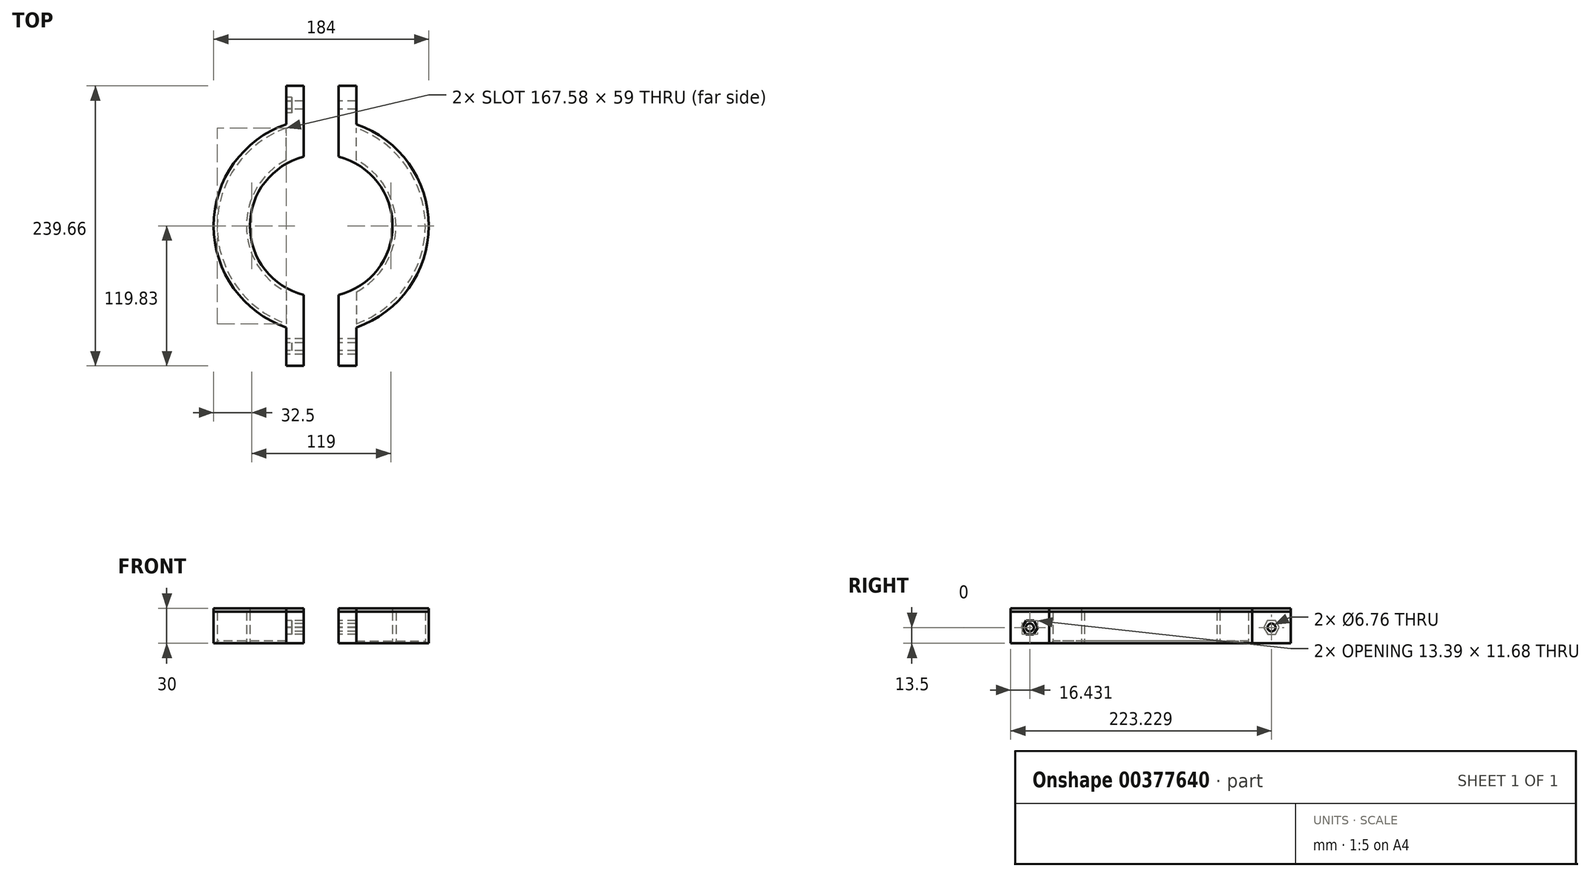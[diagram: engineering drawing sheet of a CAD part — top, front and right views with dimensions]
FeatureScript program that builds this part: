
annotation { "Feature Type Name" : "Feature", "Feature Type Description" : "" }
export const myFeature = defineFeature(function(context is Context, id is Id, definition is map)
    precondition{}
    {
        {
            var Q0;
            Q0=qCreatedBy(makeId("Top.planeOp"),FACE);
            var sketch = newSketch(context, id + "F0", { "sketchPlane" : qUnion([Q0])});
            skCircle(sketch, "E0", {"center": v(0, 0) * mm, "radius": 57 * mm, "construction": true});
            skCircle(sketch, "E1.0", {"center": v(0, 0) * mm, "radius": 61 * mm});
            skCircle(sketch, "E2.0", {"center": v(0, 0) * mm, "radius": 64 * mm});
            skCircle(sketch, "E3.0", {"center": v(0, 0) * mm, "radius": 89 * mm});
            skCircle(sketch, "E4.0", {"center": v(0, 0) * mm, "radius": 92 * mm});
            skLineSegment(sketch, "E5", {"start": v(0, 0) * mm, "end": v(0, 92) * mm, "construction": true});
            skLineSegment(sketch, "E6", {"start": v(0, 0) * mm, "end": v(0, -92) * mm, "construction": true});
            skLineSegment(sketch, "E7", {"start": v(-57, 0) * mm, "end": v(0, 0) * mm, "construction": true});
            skLineSegment(sketch, "E8", {"start": v(0, 0) * mm, "end": v(57, 0) * mm, "construction": true});
            skLineSegment(sketch, "E9", {"start": v(-15, 59.13) * mm, "end": v(-15, 90.77) * mm});
            skLineSegment(sketch, "E10", {"start": v(-30, 53.11) * mm, "end": v(-30, 86.97) * mm});
            skLineSegment(sketch, "E11", {"start": v(15, 59.13) * mm, "end": v(15, 90.77) * mm});
            skLineSegment(sketch, "E12", {"start": v(30, 53.11) * mm, "end": v(30, 86.97) * mm});
            skLineSegment(sketch, "E13", {"start": v(-30, 80.88) * mm, "end": v(-15, 80.88) * mm, "construction": true});
            skLineSegment(sketch, "E14", {"start": v(15, 80.88) * mm, "end": v(30, 80.88) * mm, "construction": true});
            skLineSegment(sketch, "E15", {"start": v(-15, 80.88) * mm, "end": v(0, 80.88) * mm, "construction": true});
            skLineSegment(sketch, "E16", {"start": v(0, 80.88) * mm, "end": v(15, 80.88) * mm, "construction": true});
            skLineSegment(sketch, "E17", {"start": v(-30, 86.97) * mm, "end": v(-30, 119.83) * mm});
            skLineSegment(sketch, "E18", {"start": v(-30, 119.83) * mm, "end": v(-15, 119.83) * mm});
            skLineSegment(sketch, "E19", {"start": v(-15, 119.83) * mm, "end": v(-15, 90.77) * mm});
            skLineSegment(sketch, "E20", {"start": v(15, 90.77) * mm, "end": v(15, 119.83) * mm});
            skLineSegment(sketch, "E21", {"start": v(15, 119.83) * mm, "end": v(30, 119.83) * mm});
            skLineSegment(sketch, "E22", {"start": v(30, 119.83) * mm, "end": v(30, 86.97) * mm});
            skLineSegment(sketch, "E23.MirrorCS", {"start": v(-15, -119.83) * mm, "end": v(-15, -90.77) * mm});
            skLineSegment(sketch, "E24.MirrorCS", {"start": v(-30, -86.97) * mm, "end": v(-30, -119.83) * mm});
            skLineSegment(sketch, "E25.MirrorCS", {"start": v(-30, -119.83) * mm, "end": v(-15, -119.83) * mm});
            skLineSegment(sketch, "E26.MirrorCS", {"start": v(15, -90.77) * mm, "end": v(15, -119.83) * mm});
            skLineSegment(sketch, "E27.MirrorCS", {"start": v(15, -119.83) * mm, "end": v(30, -119.83) * mm});
            skLineSegment(sketch, "E28.MirrorCS", {"start": v(30, -119.83) * mm, "end": v(30, -86.97) * mm});
            skLineSegment(sketch, "E29.MirrorCS", {"start": v(15, -59.13) * mm, "end": v(15, -90.77) * mm});
            skLineSegment(sketch, "E30.MirrorCS", {"start": v(30, -53.11) * mm, "end": v(30, -86.97) * mm});
            skLineSegment(sketch, "E31.MirrorCS", {"start": v(-15, -59.13) * mm, "end": v(-15, -90.77) * mm});
            skLineSegment(sketch, "E32.MirrorCS", {"start": v(-30, -53.11) * mm, "end": v(-30, -86.97) * mm});
            skSolve(sketch);
        }
        {
            var Q0;
            {var subQ0=sQuery(id+"F0.wireOp",EDGE,"E10");var subQ1=sQuery(id+"F0.wireOp",EDGE,"E2.0");var subQ2=makeQuery(id+"F0.imprint","INTERSECT",VERTEX,{"derivedFrom":[subQ1,subQ0]});Q0=makeQuery(id+"F0.imprint","IMPRINT",FACE,{"disambiguationData":[TD([[makeQuery(id+"F0.imprint","IMPRINT",EDGE,{"disambiguationData":[TD([[subQ2,-1.0]])],"derivedFrom":subQ1}),-1.0]])]});}
            var Q1;
            {var subQ0=sQuery(id+"F0.wireOp",EDGE,"E12");var subQ1=sQuery(id+"F0.wireOp",EDGE,"E2.0");var subQ2=makeQuery(id+"F0.imprint","INTERSECT",VERTEX,{"derivedFrom":[subQ1,subQ0]});Q1=makeQuery(id+"F0.imprint","IMPRINT",FACE,{"disambiguationData":[TD([[makeQuery(id+"F0.imprint","IMPRINT",EDGE,{"disambiguationData":[TD([[subQ2,1.0]])],"derivedFrom":subQ1}),-1.0]])]});}
            extrude(context, id + "F1", {"entities" : qUnion([Q0, Q1]), "oppositeDirection" : true, "depth" : 2 * mm, "offsetDistance" : 25 * mm});
        }
        {
            var Q0;
            {var subQ0=sQuery(id+"F0.wireOp",EDGE,"E10");var subQ1=sQuery(id+"F0.wireOp",EDGE,"E1.0");var subQ2=makeQuery(id+"F0.imprint","INTERSECT",VERTEX,{"derivedFrom":[subQ1,subQ0]});Q0=makeQuery(id+"F0.imprint","IMPRINT",FACE,{"disambiguationData":[TD([[makeQuery(id+"F0.imprint","IMPRINT",EDGE,{"disambiguationData":[TD([[subQ2,-1.0]])],"derivedFrom":subQ1}),-1.0]])]});}
            var Q1;
            {var subQ0=sQuery(id+"F0.wireOp",EDGE,"E9");var subQ1=sQuery(id+"F0.wireOp",EDGE,"E1.0");var subQ2=makeQuery(id+"F0.imprint","INTERSECT",VERTEX,{"derivedFrom":[subQ1,subQ0]});Q1=makeQuery(id+"F0.imprint","IMPRINT",FACE,{"disambiguationData":[TD([[makeQuery(id+"F0.imprint","IMPRINT",EDGE,{"disambiguationData":[TD([[subQ2,-1.0]])],"derivedFrom":subQ1}),-1.0]])]});}
            var Q2;
            {var subQ0=sQuery(id+"F0.wireOp",EDGE,"E11");var subQ1=sQuery(id+"F0.wireOp",EDGE,"E1.0");var subQ2=makeQuery(id+"F0.imprint","INTERSECT",VERTEX,{"derivedFrom":[subQ1,subQ0]});Q2=makeQuery(id+"F0.imprint","IMPRINT",FACE,{"disambiguationData":[TD([[makeQuery(id+"F0.imprint","IMPRINT",EDGE,{"disambiguationData":[TD([[subQ2,1.0]])],"derivedFrom":subQ1}),-1.0]])]});}
            var Q3;
            {var subQ0=sQuery(id+"F0.wireOp",EDGE,"E12");var subQ1=sQuery(id+"F0.wireOp",EDGE,"E1.0");var subQ2=makeQuery(id+"F0.imprint","INTERSECT",VERTEX,{"derivedFrom":[subQ1,subQ0]});Q3=makeQuery(id+"F0.imprint","IMPRINT",FACE,{"disambiguationData":[TD([[makeQuery(id+"F0.imprint","IMPRINT",EDGE,{"disambiguationData":[TD([[subQ2,1.0]])],"derivedFrom":subQ1}),-1.0]])]});}
            var Q4;
            {var subQ0=sQuery(id+"F0.wireOp",EDGE,"E32.MirrorCS");var subQ1=sQuery(id+"F0.wireOp",EDGE,"E2.0");var subQ2=makeQuery(id+"F0.imprint","INTERSECT",VERTEX,{"derivedFrom":[subQ1,subQ0]});Q4=makeQuery(id+"F0.imprint","IMPRINT",FACE,{"disambiguationData":[TD([[makeQuery(id+"F0.imprint","IMPRINT",EDGE,{"disambiguationData":[TD([[subQ2,-1.0]])],"derivedFrom":subQ1}),-1.0]])]});}
            var Q5;
            {var subQ0=sQuery(id+"F0.wireOp",EDGE,"E31.MirrorCS");var subQ1=sQuery(id+"F0.wireOp",EDGE,"E1.0");var subQ2=makeQuery(id+"F0.imprint","INTERSECT",VERTEX,{"derivedFrom":[subQ1,subQ0]});Q5=makeQuery(id+"F0.imprint","IMPRINT",FACE,{"disambiguationData":[TD([[makeQuery(id+"F0.imprint","IMPRINT",EDGE,{"disambiguationData":[TD([[subQ2,1.0]])],"derivedFrom":subQ1}),-1.0]])]});}
            var Q6;
            {var subQ0=sQuery(id+"F0.wireOp",EDGE,"E29.MirrorCS");var subQ1=sQuery(id+"F0.wireOp",EDGE,"E2.0");var subQ2=makeQuery(id+"F0.imprint","INTERSECT",VERTEX,{"derivedFrom":[subQ1,subQ0]});Q6=makeQuery(id+"F0.imprint","IMPRINT",FACE,{"disambiguationData":[TD([[makeQuery(id+"F0.imprint","IMPRINT",EDGE,{"disambiguationData":[TD([[subQ2,-1.0]])],"derivedFrom":subQ1}),-1.0]])]});}
            var Q7;
            {var subQ0=sQuery(id+"F0.wireOp",EDGE,"E29.MirrorCS");var subQ1=sQuery(id+"F0.wireOp",EDGE,"E1.0");var subQ2=makeQuery(id+"F0.imprint","INTERSECT",VERTEX,{"derivedFrom":[subQ1,subQ0]});Q7=makeQuery(id+"F0.imprint","IMPRINT",FACE,{"disambiguationData":[TD([[makeQuery(id+"F0.imprint","IMPRINT",EDGE,{"disambiguationData":[TD([[subQ2,-1.0]])],"derivedFrom":subQ1}),-1.0]])]});}
            var Q8;
            {var subQ0=sQuery(id+"F0.wireOp",EDGE,"E29.MirrorCS");var subQ1=sQuery(id+"F0.wireOp",EDGE,"E3.0");var subQ2=makeQuery(id+"F0.imprint","INTERSECT",VERTEX,{"derivedFrom":[subQ1,subQ0]});Q8=makeQuery(id+"F0.imprint","IMPRINT",FACE,{"disambiguationData":[TD([[makeQuery(id+"F0.imprint","IMPRINT",EDGE,{"disambiguationData":[TD([[subQ2,-1.0]])],"derivedFrom":subQ1}),-1.0]])]});}
            var Q9;
            {var subQ0=sQuery(id+"F0.wireOp",EDGE,"E32.MirrorCS");var subQ1=sQuery(id+"F0.wireOp",EDGE,"E3.0");var subQ2=makeQuery(id+"F0.imprint","INTERSECT",VERTEX,{"derivedFrom":[subQ1,subQ0]});Q9=makeQuery(id+"F0.imprint","IMPRINT",FACE,{"disambiguationData":[TD([[makeQuery(id+"F0.imprint","IMPRINT",EDGE,{"disambiguationData":[TD([[subQ2,-1.0]])],"derivedFrom":subQ1}),-1.0]])]});}
            var Q10;
            {var subQ0=sQuery(id+"F0.wireOp",EDGE,"E23.MirrorCS");Q10=makeQuery(id+"F0.imprint","IMPRINT",FACE,{"disambiguationData":[TD([[makeQuery(id+"F0.imprint","IMPRINT",EDGE,{"derivedFrom":subQ0}),1.0]])]});}
            var Q11;
            {var subQ0=sQuery(id+"F0.wireOp",EDGE,"E10");var subQ1=sQuery(id+"F0.wireOp",EDGE,"E3.0");var subQ2=makeQuery(id+"F0.imprint","INTERSECT",VERTEX,{"derivedFrom":[subQ1,subQ0]});Q11=makeQuery(id+"F0.imprint","IMPRINT",FACE,{"disambiguationData":[TD([[makeQuery(id+"F0.imprint","IMPRINT",EDGE,{"disambiguationData":[TD([[subQ2,-1.0]])],"derivedFrom":subQ1}),-1.0]])]});}
            var Q12;
            {var subQ0=sQuery(id+"F0.wireOp",EDGE,"E12");var subQ1=sQuery(id+"F0.wireOp",EDGE,"E3.0");var subQ2=makeQuery(id+"F0.imprint","INTERSECT",VERTEX,{"derivedFrom":[subQ1,subQ0]});Q12=makeQuery(id+"F0.imprint","IMPRINT",FACE,{"disambiguationData":[TD([[makeQuery(id+"F0.imprint","IMPRINT",EDGE,{"disambiguationData":[TD([[subQ2,1.0]])],"derivedFrom":subQ1}),-1.0]])]});}
            var Q13;
            {var subQ0=sQuery(id+"F0.wireOp",EDGE,"E26.MirrorCS");Q13=makeQuery(id+"F0.imprint","IMPRINT",FACE,{"disambiguationData":[TD([[makeQuery(id+"F0.imprint","IMPRINT",EDGE,{"derivedFrom":subQ0}),1.0]])]});}
            var Q14;
            {var subQ0=sQuery(id+"F0.wireOp",EDGE,"E11");var subQ1=sQuery(id+"F0.wireOp",EDGE,"E2.0");var subQ2=makeQuery(id+"F0.imprint","INTERSECT",VERTEX,{"derivedFrom":[subQ1,subQ0]});Q14=makeQuery(id+"F0.imprint","IMPRINT",FACE,{"disambiguationData":[TD([[makeQuery(id+"F0.imprint","IMPRINT",EDGE,{"disambiguationData":[TD([[subQ2,1.0]])],"derivedFrom":subQ1}),-1.0]])]});}
            var Q15;
            {var subQ0=sQuery(id+"F0.wireOp",EDGE,"E20");Q15=makeQuery(id+"F0.imprint","IMPRINT",FACE,{"disambiguationData":[TD([[makeQuery(id+"F0.imprint","IMPRINT",EDGE,{"derivedFrom":subQ0}),-1.0]])]});}
            var Q16;
            {var subQ0=sQuery(id+"F0.wireOp",EDGE,"E11");var subQ1=sQuery(id+"F0.wireOp",EDGE,"E3.0");var subQ2=makeQuery(id+"F0.imprint","INTERSECT",VERTEX,{"derivedFrom":[subQ1,subQ0]});Q16=makeQuery(id+"F0.imprint","IMPRINT",FACE,{"disambiguationData":[TD([[makeQuery(id+"F0.imprint","IMPRINT",EDGE,{"disambiguationData":[TD([[subQ2,1.0]])],"derivedFrom":subQ1}),-1.0]])]});}
            var Q17;
            {var subQ0=sQuery(id+"F0.wireOp",EDGE,"E9");var subQ1=sQuery(id+"F0.wireOp",EDGE,"E2.0");var subQ2=makeQuery(id+"F0.imprint","INTERSECT",VERTEX,{"derivedFrom":[subQ1,subQ0]});Q17=makeQuery(id+"F0.imprint","IMPRINT",FACE,{"disambiguationData":[TD([[makeQuery(id+"F0.imprint","IMPRINT",EDGE,{"disambiguationData":[TD([[subQ2,-1.0]])],"derivedFrom":subQ1}),-1.0]])]});}
            var Q18;
            {var subQ0=sQuery(id+"F0.wireOp",EDGE,"E9");var subQ1=sQuery(id+"F0.wireOp",EDGE,"E3.0");var subQ2=makeQuery(id+"F0.imprint","INTERSECT",VERTEX,{"derivedFrom":[subQ1,subQ0]});Q18=makeQuery(id+"F0.imprint","IMPRINT",FACE,{"disambiguationData":[TD([[makeQuery(id+"F0.imprint","IMPRINT",EDGE,{"disambiguationData":[TD([[subQ2,-1.0]])],"derivedFrom":subQ1}),-1.0]])]});}
            var Q19;
            {var subQ2=sQuery(id+"F0.wireOp",EDGE,"E17");Q19=makeQuery(id+"F0.imprint","IMPRINT",FACE,{"disambiguationData":[TD([[makeQuery(id+"F0.imprint","IMPRINT",EDGE,{"derivedFrom":subQ2}),-1.0]])]});}
            extrude(context, id + "F2", {"entities" : qUnion([Q0, Q1, Q2, Q3, Q4, Q5, Q6, Q7, Q8, Q9, Q10, Q11, Q12, Q13, Q14, Q15, Q16, Q17, Q18, Q19]), "depth" : 25 * mm, "offsetDistance" : 25 * mm, "hasSecondDirection" : true, "secondDirectionOppositeDirection" : true, "secondDirectionDepth" : 2 * mm});
        }
        {
            var Q0;
            Q0=qCreatedBy(makeId("Right.planeOp"),FACE);
            var sketch = newSketch(context, id + "F3", { "sketchPlane" : qUnion([Q0])});
            skLineSegment(sketch, "E33", {"start": v(0, 0) * mm, "end": v(0, -64.4) * mm, "construction": true});
            skLineSegment(sketch, "E34", {"start": v(0, 0) * mm, "end": v(0, 59.15) * mm, "construction": true});
            skSolve(sketch);
        }
        {
            var Q0;
            Q0=makeQuery(id+"F2.opExtrude","SWEPT_FACE",FACE,{"disambiguationData":[OSD([sQuery(id+"F0.wireOp",EDGE,"E17")])]});
            var sketch = newSketch(context, id + "F4", { "sketchPlane" : qUnion([Q0])});
            skCircle(sketch, "E35", {"center": v(-103.4, 11.5) * mm, "radius": 3.38 * mm});
            skPoint(sketch, "E35.centerSnap0", {"position": v(-103.4, 25) * mm});
            skPoint(sketch, "E35.centerSnap1", {"position": v(-119.83, 11.5) * mm});
            skCircle(sketch, "E36.cCircle", {"center": v(-103.4, 11.5) * mm, "radius": 6.7 * mm, "construction": true});
            skLineSegment(sketch, "E36.0", {"start": v(-99.98, 17.26) * mm, "end": v(-96.7, 11.42) * mm});
            skLineSegment(sketch, "E36.1", {"start": v(-96.7, 11.42) * mm, "end": v(-100.12, 5.66) * mm});
            skLineSegment(sketch, "E36.2", {"start": v(-100.12, 5.66) * mm, "end": v(-106.82, 5.74) * mm});
            skLineSegment(sketch, "E36.3", {"start": v(-106.82, 5.74) * mm, "end": v(-110.1, 11.58) * mm});
            skLineSegment(sketch, "E36.4", {"start": v(-110.1, 11.58) * mm, "end": v(-106.68, 17.34) * mm});
            skLineSegment(sketch, "E36.5", {"start": v(-106.68, 17.34) * mm, "end": v(-99.98, 17.26) * mm});
            skCircle(sketch, "E37.MirrorC", {"center": v(103.4, 11.5) * mm, "radius": 3.38 * mm});
            skLineSegment(sketch, "E38.MirrorCS", {"start": v(99.98, 17.26) * mm, "end": v(96.7, 11.42) * mm});
            skLineSegment(sketch, "E39.MirrorCS", {"start": v(96.7, 11.42) * mm, "end": v(100.12, 5.66) * mm});
            skLineSegment(sketch, "E40.MirrorCS", {"start": v(100.12, 5.66) * mm, "end": v(106.82, 5.74) * mm});
            skLineSegment(sketch, "E41.MirrorCS", {"start": v(106.82, 5.74) * mm, "end": v(110.1, 11.58) * mm});
            skLineSegment(sketch, "E42.MirrorCS", {"start": v(110.1, 11.58) * mm, "end": v(106.68, 17.34) * mm});
            skLineSegment(sketch, "E43.MirrorCS", {"start": v(106.68, 17.34) * mm, "end": v(99.98, 17.26) * mm});
            skCircle(sketch, "E44.MirrorC", {"center": v(103.4, 11.5) * mm, "radius": 6.7 * mm, "construction": true});
            skSolve(sketch);
        }
        {
            var Q0;
            Q0=makeQuery(id+"F4.imprint","IMPRINT",FACE,{"disambiguationData":[TD([[makeQuery(id+"F4.imprint","IMPRINT",EDGE,{"derivedFrom":sQuery(id+"F4.wireOp",EDGE,"E35")}),1.0]])]});
            var Q1;
            Q1=makeQuery(id+"F4.imprint","IMPRINT",FACE,{"disambiguationData":[TD([[makeQuery(id+"F4.imprint","IMPRINT",EDGE,{"derivedFrom":sQuery(id+"F4.wireOp",EDGE,"E37.MirrorC")}),-1.0]])]});
            extrude(context, id + "F5", {"entities" : qUnion([Q0, Q1]), "operationType" : NewBodyOperationType.REMOVE, "endBound" : BoundingType.THROUGH_ALL, "oppositeDirection" : true, "depth" : 25 * mm, "offsetDistance" : 25 * mm});
        }
        {
            var Q0;
            Q0=makeQuery(id+"F2.opExtrude","SWEPT_FACE",FACE,{"disambiguationData":[OSD([sQuery(id+"F0.wireOp",EDGE,"E28.MirrorCS")])]});
            var sketch = newSketch(context, id + "F6", { "sketchPlane" : qUnion([Q0])});
            skCircle(sketch, "E45", {"center": v(-103.4, 11.5) * mm, "radius": 5 * mm});
            skCircle(sketch, "E46.MirrorC", {"center": v(103.4, 11.5) * mm, "radius": 5 * mm});
            skSolve(sketch);
        }
        {
            var Q0;
            Q0=makeQuery(id+"F4.imprint","IMPRINT",FACE,{"disambiguationData":[TD([[makeQuery(id+"F4.imprint","IMPRINT",EDGE,{"derivedFrom":sQuery(id+"F4.wireOp",EDGE,"E35")}),-1.0]])]});
            var Q1;
            Q1=makeQuery(id+"F4.imprint","IMPRINT",FACE,{"disambiguationData":[TD([[makeQuery(id+"F4.imprint","IMPRINT",EDGE,{"derivedFrom":sQuery(id+"F4.wireOp",EDGE,"E37.MirrorC")}),1.0]])]});
            extrude(context, id + "F7", {"entities" : qUnion([Q0, Q1]), "operationType" : NewBodyOperationType.REMOVE, "oppositeDirection" : true, "depth" : 5 * mm, "offsetDistance" : 25 * mm});
        }
        {
            var Q0;
            Q0=makeQuery(id+"F2.opExtrude","CAP_FACE",FACE,{"disambiguationData":[OSD([sQuery(id+"F0.wireOp",EDGE,"E1.0"),sQuery(id+"F0.wireOp",EDGE,"E2.0"),sQuery(id+"F0.wireOp",EDGE,"E3.0"),sQuery(id+"F0.wireOp",EDGE,"E4.0"),sQuery(id+"F0.wireOp",EDGE,"E9"),sQuery(id+"F0.wireOp",EDGE,"E10"),sQuery(id+"F0.wireOp",EDGE,"E17"),sQuery(id+"F0.wireOp",EDGE,"E18"),sQuery(id+"F0.wireOp",EDGE,"E19"),sQuery(id+"F0.wireOp",EDGE,"E23.MirrorCS"),sQuery(id+"F0.wireOp",EDGE,"E24.MirrorCS"),sQuery(id+"F0.wireOp",EDGE,"E25.MirrorCS"),sQuery(id+"F0.wireOp",EDGE,"E31.MirrorCS"),sQuery(id+"F0.wireOp",EDGE,"E32.MirrorCS")])],"isStart":false});
            var sketch = newSketch(context, id + "F8", { "sketchPlane" : qUnion([Q0])});
            skLineSegment(sketch, "E47.1.0", {"start": v(30, 119.83) * mm, "end": v(15, 119.83) * mm});
            skLineSegment(sketch, "E47.1.1", {"start": v(15, 119.83) * mm, "end": v(15, 59.13) * mm});
            skArc(sketch, "E47.1.2", {"start": v(15, 59.13) * mm, "mid": v(61, 0) * mm, "end": v(15, -59.13) * mm});
            skLineSegment(sketch, "E47.1.3", {"start": v(15, -59.13) * mm, "end": v(15, -119.83) * mm});
            skLineSegment(sketch, "E47.1.4", {"start": v(15, -119.83) * mm, "end": v(30, -119.83) * mm});
            skLineSegment(sketch, "E47.1.5", {"start": v(30, -119.83) * mm, "end": v(30, -86.97) * mm});
            skArc(sketch, "E47.1.6", {"start": v(30, -86.97) * mm, "mid": v(92, 0) * mm, "end": v(30, 86.97) * mm});
            skLineSegment(sketch, "E47.1.7", {"start": v(30, 86.97) * mm, "end": v(30, 119.83) * mm});
            skLineSegment(sketch, "E48.MirrorCS", {"start": v(-15, 119.83) * mm, "end": v(-15, 59.13) * mm});
            skLineSegment(sketch, "E49.MirrorCS", {"start": v(-30, 119.83) * mm, "end": v(-15, 119.83) * mm});
            skLineSegment(sketch, "E50.MirrorCS", {"start": v(-30, 86.97) * mm, "end": v(-30, 119.83) * mm});
            skArc(sketch, "E51.MirrorCS", {"start": v(-30, -86.97) * mm, "mid": v(-92, 0) * mm, "end": v(-30, 86.97) * mm});
            skArc(sketch, "E52.MirrorCS", {"start": v(-15, 59.13) * mm, "mid": v(-61, 0) * mm, "end": v(-15, -59.13) * mm});
            skLineSegment(sketch, "E53.MirrorCS", {"start": v(-15, -59.13) * mm, "end": v(-15, -119.83) * mm});
            skLineSegment(sketch, "E54.MirrorCS", {"start": v(-15, -119.83) * mm, "end": v(-30, -119.83) * mm});
            skLineSegment(sketch, "E55.MirrorCS", {"start": v(-30, -119.83) * mm, "end": v(-30, -86.97) * mm});
            skSolve(sketch);
        }
        {
            var Q0;
            Q0=makeQuery(id+"F8.imprint","IMPRINT",FACE,{"disambiguationData":[TD([[makeQuery(id+"F8.imprint","IMPRINT",EDGE,{"derivedFrom":sQuery(id+"F8.wireOp",EDGE,"E48.MirrorCS")}),1.0]])]});
            var Q1;
            Q1=makeQuery(id+"F8.imprint","IMPRINT",FACE,{"disambiguationData":[TD([[makeQuery(id+"F8.imprint","IMPRINT",EDGE,{"derivedFrom":sQuery(id+"F8.wireOp",EDGE,"E47.1.0")}),1.0]])]});
            var Q2;
            {var subQ0=sQuery(id+"F0.wireOp",EDGE,"E10");Q2=makeQuery(id+"F8.imprint","IMPRINT",FACE,{"disambiguationData":[TD([[makeQuery(id+"F8.imprint","IMPRINT",EDGE,{"derivedFrom":makeQuery(id+"F2.opExtrude","CAP_EDGE",EDGE,{"disambiguationData":[OSD([subQ0])],"isStart":false})}),1.0]])]});}
            extrude(context, id + "F9", {"entities" : qUnion([Q0, Q1, Q2]), "depth" : 3 * mm, "offsetDistance" : 25 * mm});
        }
        {
            var Q0;
            Q0=makeQuery(id+"F6.imprint","IMPRINT",FACE,{"disambiguationData":[TD([[makeQuery(id+"F6.imprint","IMPRINT",EDGE,{"derivedFrom":sQuery(id+"F6.wireOp",EDGE,"E45")}),1.0]])]});
            var Q1;
            Q1=makeQuery(id+"F6.imprint","IMPRINT",FACE,{"disambiguationData":[TD([[makeQuery(id+"F6.imprint","IMPRINT",EDGE,{"derivedFrom":sQuery(id+"F6.wireOp",EDGE,"E46.MirrorC")}),-1.0]])]});
            extrude(context, id + "F10", {"entities" : qUnion([Q0, Q1]), "operationType" : NewBodyOperationType.REMOVE, "oppositeDirection" : true, "depth" : 5 * mm, "offsetDistance" : 25 * mm});
        }
    });
